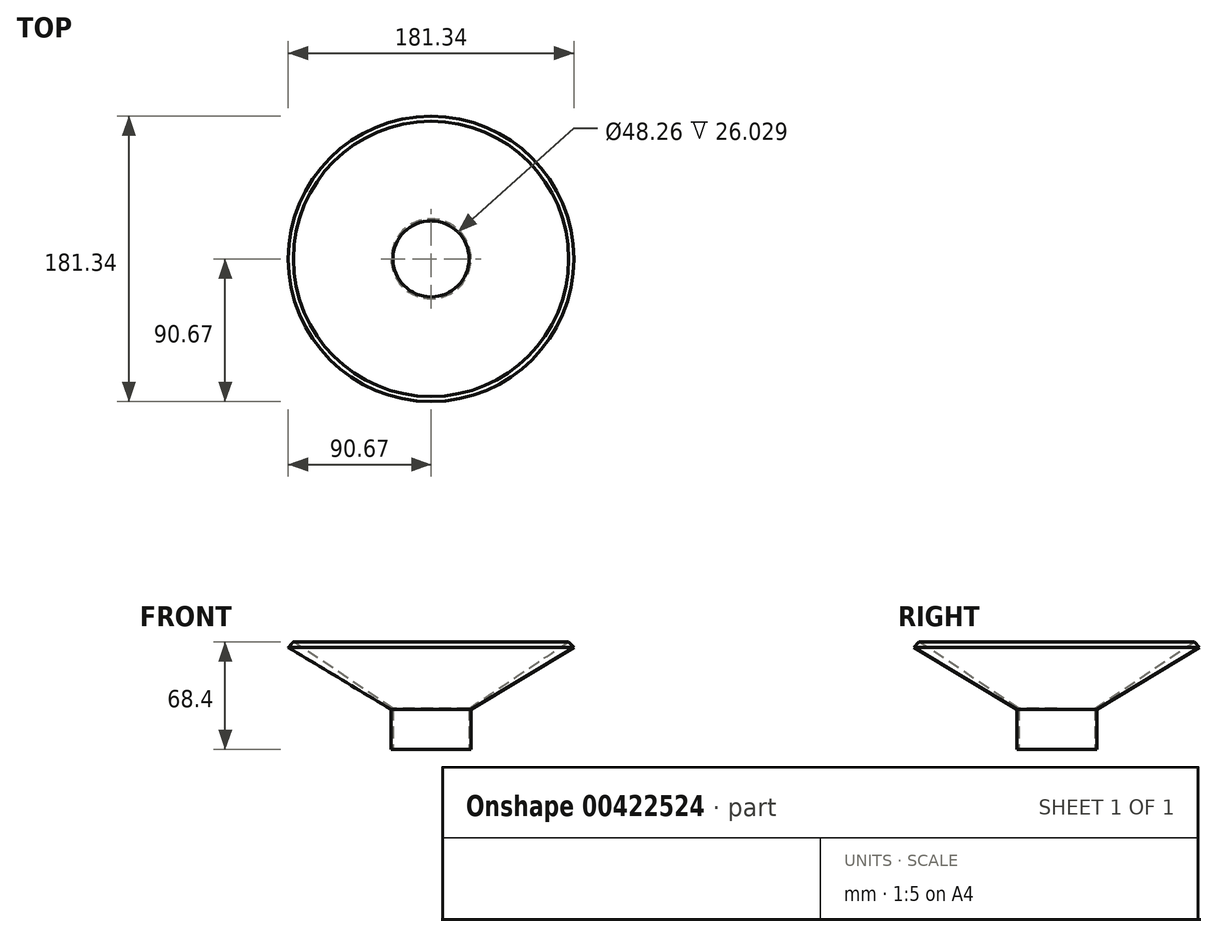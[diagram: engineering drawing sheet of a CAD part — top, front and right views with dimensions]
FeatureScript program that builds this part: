
annotation { "Feature Type Name" : "Feature", "Feature Type Description" : "" }
export const myFeature = defineFeature(function(context is Context, id is Id, definition is map)
    precondition{}
    {
        {
            var Q0;
            Q0=qCreatedBy(makeId("Front.planeOp"),FACE);
            var sketch = newSketch(context, id + "F0", { "sketchPlane" : qUnion([Q0])});
            skLineSegment(sketch, "E0.bottom", {"start": v(0, 0) * mm, "end": v(-25.4, 0) * mm});
            skLineSegment(sketch, "E0.left", {"start": v(0, 0) * mm, "end": v(0, 25.4) * mm});
            skLineSegment(sketch, "E0.right", {"start": v(-25.4, 0) * mm, "end": v(-25.4, 25.4) * mm});
            skLineSegment(sketch, "E1", {"start": v(0, 25.4) * mm, "end": v(65.27, 64.73) * mm});
            skLineSegment(sketch, "E2", {"start": v(62.03, 68.4) * mm, "end": v(65.27, 64.73) * mm});
            skLineSegment(sketch, "E3", {"start": v(-25.4, 25.4) * mm, "end": v(-2.21, 25.4) * mm});
            skLineSegment(sketch, "E4", {"start": v(-2.21, 25.4) * mm, "end": v(62.03, 68.4) * mm});
            skSolve(sketch);
        }
        {
            var Q0;
            Q0=makeQuery(id+"F0.imprint","IMPRINT",FACE,{"disambiguationData":[TD([[makeQuery(id+"F0.imprint","IMPRINT",EDGE,{"derivedFrom":sQuery(id+"F0.wireOp",EDGE,"E0.bottom")}),-1.0]])]});
            var Q1;
            Q1=sQuery(id+"F0.wireOp",EDGE,"E0.right");
            revolve(context, id + "F1", {"entities" : qUnion([Q0]), "axis" : qUnion([Q1]), "revolveType" : RevolveType.FULL});
        }
        {
            var Q0;
            Q0=makeQuery(id+"F1.opRevolve","SWEPT_FACE",FACE,{"disambiguationData":[OSD([sQuery(id+"F0.wireOp",EDGE,"E0.bottom")])]});
            var sketch = newSketch(context, id + "F2", { "sketchPlane" : qUnion([Q0])});
            skCircle(sketch, "E5", {"center": v(-25.4, 0) * mm, "radius": 24.13 * mm});
            skSolve(sketch);
        }
        {
            var Q0;
            Q0 = qSketchRegion(id + "F2", true);
            extrude(context, id + "F3", {"entities" : qUnion([Q0]), "operationType" : NewBodyOperationType.REMOVE, "oppositeDirection" : true, "depth" : 762 * mm});
        }
    });
